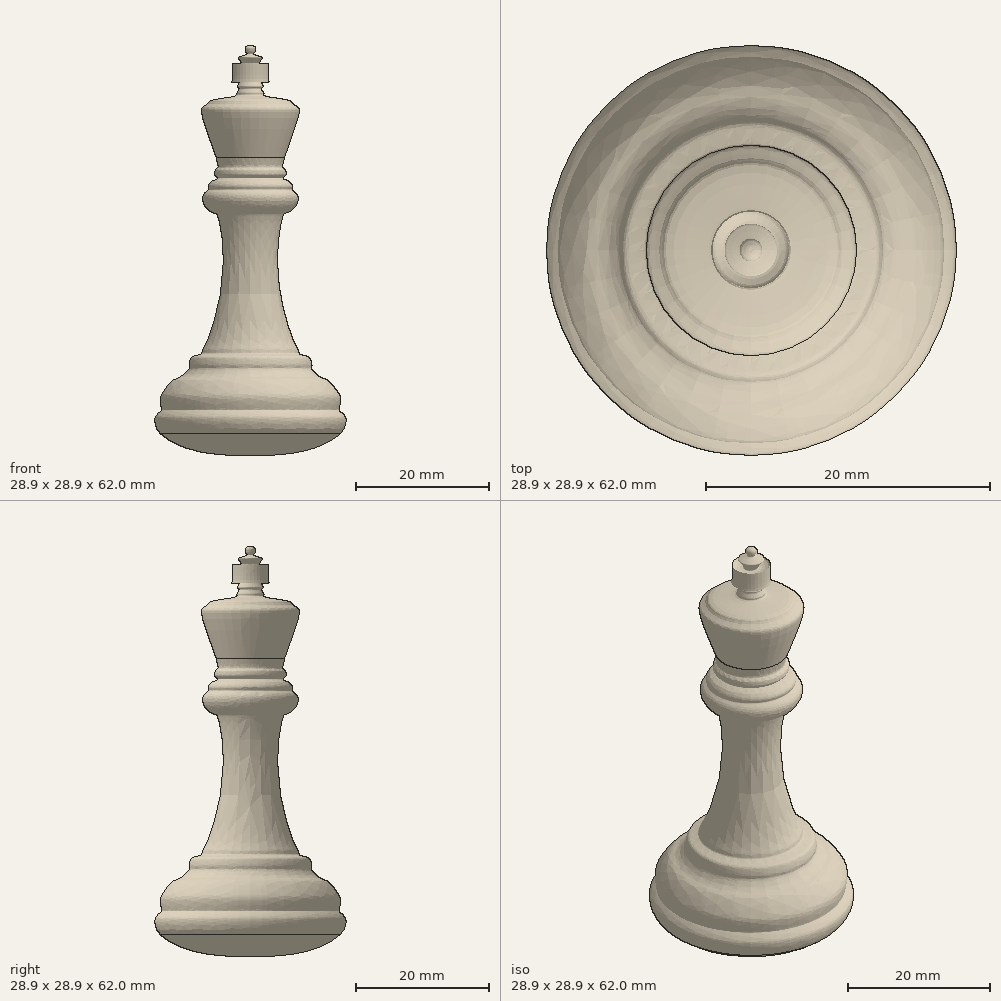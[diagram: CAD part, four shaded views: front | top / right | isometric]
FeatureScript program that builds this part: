
annotation { "Feature Type Name" : "Feature", "Feature Type Description" : "" }
export const myFeature = defineFeature(function(context is Context, id is Id, definition is map)
    precondition{}
    {
        {
            var Q0;
            Q0=qCreatedBy(makeId("Front.planeOp"),FACE);
            var sketch = newSketch(context, id + "F0", { "sketchPlane" : qUnion([Q0])});
            skLineSegment(sketch, "E0", {"start": v(0, 28.6) * mm, "end": v(0, -33.4) * mm});
            skFitSpline(sketch, "E1", {"points": [v(0, -33.4) * mm, v(2.54, -33.4) * mm, v(8.93, -32.54) * mm, v(13.62, -30.12) * mm, v(14.37, -28.84) * mm, v(14.47, -28.02) * mm, v(14.25, -27.39) * mm, v(13.46, -26.66) * mm, v(13.4, -26.6) * mm, v(13.56, -25.79) * mm, v(13.62, -24.66) * mm, v(13.16, -23.7) * mm, v(11.6, -22) * mm, v(10.5, -21.5) * mm, v(9.3, -20.32) * mm, v(9.31, -19.88) * mm, v(9.16, -19.06) * mm, v(8.75, -18.47) * mm, v(7.45, -18.04) * mm, v(7.3, -17.55) * mm, v(6.78, -16.63) * mm, v(4.87, -10.61) * mm, v(4.1, -4.03) * mm, v(4.5, 0.97) * mm, v(4.99, 2.9) * mm, v(5.19, 3.17) * mm, v(5.95, 3.42) * mm, v(6.63, 3.95) * mm, v(7.14, 4.82) * mm, v(7.19, 5.8) * mm, v(6.66, 6.5) * mm, v(6.3, 6.74) * mm, v(6.4, 7.07) * mm, v(6.33, 7.54) * mm, v(5.51, 8.24) * mm, v(4.9, 8.45) * mm, v(5.1, 8.63) * mm, v(5.4, 9) * mm, v(5.42, 9.37) * mm, v(5.25, 9.85) * mm, v(4.94, 10.1) * mm, v(5.2, 11.68) * mm], "startDerivative": vector(63.26, -1.25) * mm, "endDerivative": vector(21.25, 71.33) * mm});
            skFitSpline(sketch, "E2", {"points": [v(5.2, 11.68) * mm, v(7.4, 18.46) * mm, v(7.22, 19.26) * mm, v(6.4, 19.8) * mm, v(5.98, 20.26) * mm, v(2.1, 21.05) * mm, v(2.05, 21.28) * mm, v(1.95, 21.56) * mm, v(1.7, 22.08) * mm, v(1.99, 22.29) * mm, v(1.89, 22.63) * mm, v(1.43, 23.55) * mm, v(2.75, 23.04) * mm, v(2.76, 23.37) * mm, v(2.7, 25.84) * mm, v(2.53, 25.62) * mm, v(1.06, 25.3) * mm, v(1.07, 25.57) * mm, v(1.79, 26.6) * mm, v(1.8, 26.83) * mm, v(0.53, 27.28) * mm, v(0.6, 27.42) * mm, v(0.79, 27.86) * mm, v(0.71, 28.36) * mm, v(0.22, 28.6) * mm, v(0, 28.6) * mm], "startDerivative": vector(26.08, 71.5) * mm, "endDerivative": vector(-9.26, -1.12) * mm});
            skFitSpline(sketch, "E3", {"points": [v(13.62, -30.12) * mm, v(10.87, -30.63) * mm, v(5.78, -30.86) * mm, v(0, -30.98) * mm], "startDerivative": vector(-9.6, -2.19) * mm, "endDerivative": vector(-15.19, -0.3) * mm});
            skSolve(sketch);
        }
        {
            var Q0;
            Q0 = qSketchRegion(id + "F0", true);
            var Q1;
            Q1=sQuery(id+"F0.wireOp",EDGE,"E0");
            revolve(context, id + "F1", {"entities" : qUnion([Q0]), "axis" : qUnion([Q1]), "revolveType" : RevolveType.FULL});
        }
    });
